# Revit family: Shower_Head-Grohe-Rainshower-26644000
name_source: partatom
category: Plumbing Fixtures
revit_build: Autodesk Revit 2014 (Build: 20130308_1515(x64)
units: mm (PartAtom-declared; Revit-internal decimal feet)

## types (1)
- 26644000
    Assembly Code = D2010700
    CW Connection = Yes
    CWFU = 3
    Cold Water Connection Diameter = 1/2"
    Cold Water Connection Radius = 1/4"
    Default Elevation = 0"
    Description = Rainshower™ SmartConnect 310 Showerhead with Remote, Round
    Finish = Brass-Grohe-000-Starlight Chrome
    Flow Rate = 1.75 gpm (6.6 Lpm)
    HW Connection = Yes
    HWFU = 3
    Height = 2 5/8"
    Hot Water Connection Diameter = 1"
    Hot Water Connection Radius = 1/4"
    Manufacturer = Grohe
    Material = Brass-Grohe-000-Starlight Chrome
    Model = 26644000
    Price = Prices may vary. Please consult Manufacturer Representative for most up-to-date price list.
    Tempered Water Connection Diameter = 1/2"
    Tempered Water Connection Radius = 1/4"
    URL = https://www.grohe.us
    Vent Connection = No
    WFU = 4
    Warranty Documentation Link = https://www.grohe.us
    Waste Connection = No
    Width = 12 3/16"

## geometry (parser evidence)
native form markers: Sweep x1
no freeform markers — native parametric forms only
